# Revit family: Accessory-Tray-KOHLER-Draft-K-27366
name_source: partatom
category: Specialty Equipment
revit_build: Autodesk Revit 2017 (Build: 20160225_1515(x64)
units: mm (PartAtom-declared; Revit-internal decimal feet)

## family parameters
Cut with Voids When Loaded = No
Host = Face
OmniClass Number = 23.31.25.00
Part Type = Normal
Room Calculation Point = No
Round Connector Dimension = Use Diameter
Shared = No

## types (2) — shared parameters
ADA Compliant = No
Assembly Code = C1030200
Date Modified = 03/30/2020
Default Elevation = 42"
Description = 12inch holder
Height = 4 11/16"
Length = 3/4"
Manufacturer = KOHLER Co.
Master Format 2014 = 10 28 00
Master Format 2014 Name = Toilet, Bath, and Laundry Accessories
Material = Durable Composite Material
Product Documentation Link = https://www.us.kohler.com
Product Name = Draft
Product Page URL = http://www.us.kohler.com
URL = https://www.us.kohler.com
WaterSense Certified = No
Width = 11 13/16"

## per-type parameters (varying)
| type | Finish | Model | Type |
| 0-White | Kohler-Plastic-0-White | K-27366-0 | 1 |
| 7-Black Black | Kohler-Plastic-7-Black_Black | K-27366-7 | 2 |

## geometry (parser evidence)
native form markers: Sweep x6
no freeform markers — native parametric forms only
